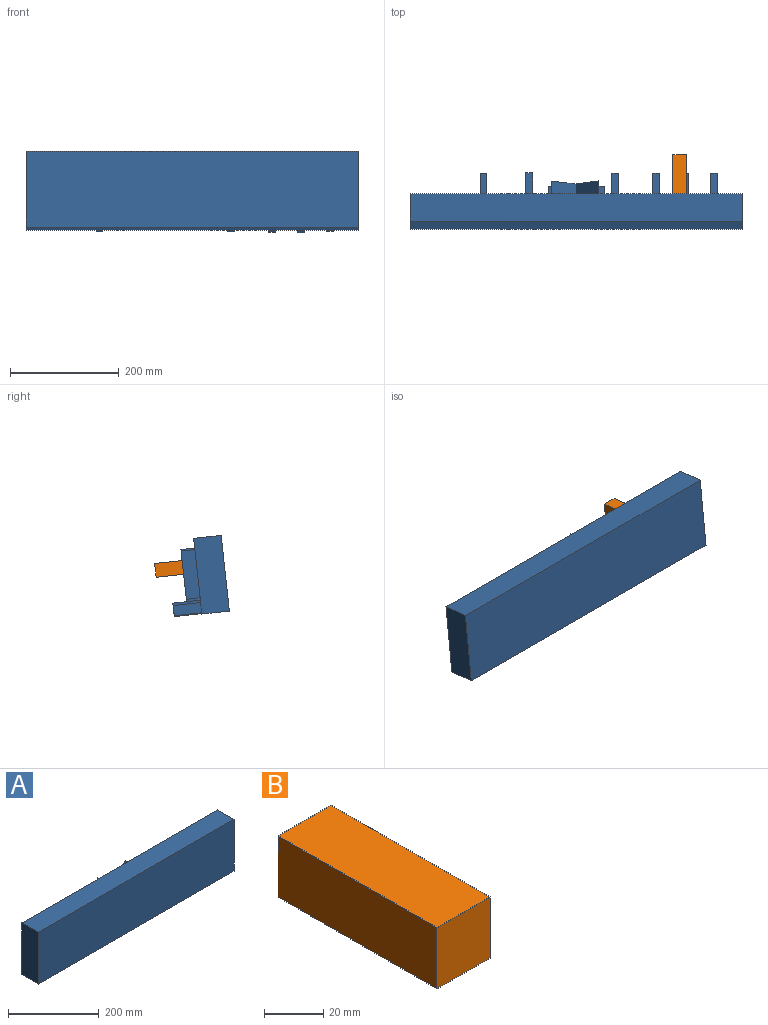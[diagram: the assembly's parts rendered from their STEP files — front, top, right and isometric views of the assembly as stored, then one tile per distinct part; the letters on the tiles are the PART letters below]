
ASSEMBLY  parts=2 mates=1
PART A: 55 faces, bbox 609.6x101.6x139.7 mm
  f0: plane 609.6x139.7mm, normal (0,1,0), area 80574.3mm2, adj f1,f2,f3,f4,f6,f7,f8,f9
  f1: plane 609.6x50.8mm, normal (0,0,-1), area 30967.7mm2, adj f0,f2,f4,f5
  f2: plane 139.7x50.8mm, normal (1,0,0), area 7096.8mm2, adj f0,f1,f3,f5
  f3: plane 609.6x50.8mm, normal (0,0,1), area 30967.7mm2, adj f0,f2,f4,f5
  f4: plane 139.7x50.8mm, normal (-1,0,0), area 7096.8mm2, adj f0,f1,f3,f5
  f5: plane 609.6x139.7mm, normal (0,-1,0), area 85161.1mm2, adj f1,f2,f3,f4
  f6: plane 25.4x6.04mm, normal (0,0,1), area 153.4mm2, adj f0,f7,f23,f24
  f7: plane 25.4x10.83mm, normal (-1,0,0), area 275mm2, adj f0,f6,f8,f24
  f8: plane 25.4x22.68mm, normal (0,0,-1), area 576.1mm2, adj f0,f7,f9,f24
  f9: plane 25.4x10.6mm, normal (1,0,0), area 269.2mm2, adj f0,f8,f10,f24
  f10: plane 25.4x7.86mm, normal (0,0,1), area 199.8mm2, adj f0,f9,f11,f24
  f11: plane 69.18x25.4mm, normal (1,0,0), area 1757.2mm2, adj f0,f10,f12,f24
  f12: plane 42.85x36.19mm, normal (-0.76,0,-0.65), area 1424.7mm2, adj f0,f11,f13,f24
  f13: plane 41.26x30.94mm, normal (0.8,0,-0.6), area 1310mm2, adj f0,f12,f14,f24
  f14: plane 66.79x25.4mm, normal (-1,0,0), area 1696.4mm2, adj f0,f13,f15,f24
  f15: plane 25.4x10.49mm, normal (0,0,1), area 266.3mm2, adj f0,f14,f16,f24
  f16: plane 25.4x12.54mm, normal (-1,0,0), area 318.4mm2, adj f0,f15,f17,f24
  f17: plane 31.91x25.4mm, normal (0,0,-1), area 810.6mm2, adj f0,f16,f18,f24
  f18: plane 25.4x12.65mm, normal (1,0,0), area 321.3mm2, adj f0,f17,f19,f24
  f19: plane 25.4x10.26mm, normal (0,0,1), area 260.5mm2, adj f0,f18,f20,f24
  f20: plane 91.18x25.4mm, normal (1,0,0), area 2316mm2, adj f0,f19,f21,f24
  f21: plane 52.14x42.11mm, normal (-0.78,0,0.63), area 1702.4mm2, adj f0,f20,f22,f24
  f22: plane 49.18x44.96mm, normal (0.74,0,0.67), area 1692.5mm2, adj f0,f21,f23,f24
  f23: plane 88.9x25.4mm, normal (-1,0,0), area 2258.1mm2, adj f0,f6,f22,f24
  f24: plane 103.83x103.37mm, normal (0,1,0), area 3135.2mm2, adj f6,f7,f8,f9,f10,f11,f12,f13
  f25: plane 50.8x12.7mm, normal (0,0,1), area 645.2mm2, adj f0,f26,f28,f29
  f26: plane 50.8x19.05mm, normal (1,0,0), area 967.7mm2, adj f0,f25,f27,f29
  f27: plane 50.8x12.7mm, normal (0,0,-1), area 645.2mm2, adj f0,f26,f28,f29
  f28: plane 50.8x19.05mm, normal (-1,0,0), area 967.7mm2, adj f0,f25,f27,f29
  f29: plane 19.05x12.7mm, normal (0,1,0), area 241.9mm2, adj f25,f26,f27,f28
  f30: plane 50.8x12.7mm, normal (0,0,1), area 645.2mm2, adj f0,f31,f33,f34
  f31: plane 50.8x19.05mm, normal (1,0,0), area 967.7mm2, adj f0,f30,f32,f34
  f32: plane 50.8x12.7mm, normal (0,0,-1), area 645.2mm2, adj f0,f31,f33,f34
  f33: plane 50.8x19.05mm, normal (-1,0,0), area 967.7mm2, adj f0,f30,f32,f34
  f34: plane 19.05x12.7mm, normal (0,1,0), area 241.9mm2, adj f30,f31,f32,f33
  f35: plane 50.8x12.7mm, normal (0,0,1), area 645.2mm2, adj f0,f36,f38,f39
  f36: plane 50.8x19.05mm, normal (1,0,0), area 967.7mm2, adj f0,f35,f37,f39
  f37: plane 50.8x12.7mm, normal (0,0,-1), area 645.2mm2, adj f0,f36,f38,f39
  f38: plane 50.8x19.05mm, normal (-1,0,0), area 967.7mm2, adj f0,f35,f37,f39
  f39: plane 19.05x12.7mm, normal (0,1,0), area 241.9mm2, adj f35,f36,f37,f38
  f40: plane 50.8x12.7mm, normal (0,0,1), area 645.2mm2, adj f0,f41,f43,f44
  f41: plane 50.8x19.05mm, normal (1,0,0), area 967.7mm2, adj f0,f40,f42,f44
  f42: plane 50.8x12.7mm, normal (0,0,-1), area 645.2mm2, adj f0,f41,f43,f44
  f43: plane 50.8x19.05mm, normal (-1,0,0), area 967.7mm2, adj f0,f40,f42,f44
  f44: plane 19.05x12.7mm, normal (0,1,0), area 241.9mm2, adj f40,f41,f42,f43
  f45: plane 50.8x12.7mm, normal (0,0,1), area 645.2mm2, adj f0,f46,f48,f49
  f46: plane 50.8x19.05mm, normal (1,0,0), area 967.7mm2, adj f0,f45,f47,f49
  f47: plane 50.8x12.7mm, normal (0,0,-1), area 645.2mm2, adj f0,f46,f48,f49
  f48: plane 50.8x19.05mm, normal (-1,0,0), area 967.7mm2, adj f0,f45,f47,f49
  f49: plane 19.05x12.7mm, normal (0,1,0), area 241.9mm2, adj f45,f46,f47,f48
  f50: plane 50.8x12.7mm, normal (0,0,1), area 645.2mm2, adj f0,f51,f53,f54
  f51: plane 50.8x19.05mm, normal (1,0,0), area 967.7mm2, adj f0,f50,f52,f54
  f52: plane 50.8x12.7mm, normal (0,0,-1), area 645.2mm2, adj f0,f51,f53,f54
  f53: plane 50.8x19.05mm, normal (-1,0,0), area 967.7mm2, adj f0,f50,f52,f54
  f54: plane 19.05x12.7mm, normal (0,1,0), area 241.9mm2, adj f50,f51,f52,f53
PART B: 6 faces, bbox 25.4x76.2x25.4 mm
  f0: plane 76.2x25.4mm, normal (0,0,1), area 1935.5mm2, adj f1,f3,f4,f5
  f1: plane 76.2x25.4mm, normal (-1,0,0), area 1935.5mm2, adj f0,f2,f4,f5
  f2: plane 76.2x25.4mm, normal (0,0,-1), area 1935.5mm2, adj f1,f3,f4,f5
  f3: plane 76.2x25.4mm, normal (1,0,0), area 1935.5mm2, adj f0,f2,f4,f5
  f4: plane 25.4x25.4mm, normal (0,-1,0), area 645.2mm2, adj f0,f1,f2,f3
  f5: plane 25.4x25.4mm, normal (0,1,0), area 645.2mm2, adj f0,f1,f2,f3
PLACE A rot(axis=(-1,0,0),6.2deg) t=(-231.24,136.07,-78.7)mm
PLACE B rot(axis=(-1,0,0),6.2deg) t=(-53.44,215.26,-55.38)mm
MATE fastened A.f0 <-> B.f4  axis (0,0.99,-0.11) through (73.56,128.52,-148.14)mm
